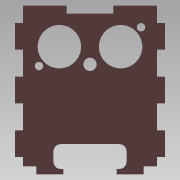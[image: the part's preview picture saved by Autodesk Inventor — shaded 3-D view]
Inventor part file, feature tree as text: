
AUTODESK INVENTOR PART (.ipt)
format: ipt  version: 2015 SP1 (Build 190203100, 203)  size: 165,888 bytes
history: native  units: mm
features: extrude x1, sketch x1
ambient origin geometry x8: Origin, YZ Plane, XZ Plane, XY Plane, X Axis, Y Axis, Z Axis, Center Point
bodies: Solid1 (feature_tree)
feature tree (2):
  extrude  "Extrusion1"  Depth=3.0mm
  sketch  "Sketch1"  dims[d0=10.0mm d1=3.0mm d2=20.0mm d4=15.0mm d5=20.0mm d7=15.0mm d14=10.0mm d15=90.0deg d16=20.0mm d18=20.0mm d19=20.0mm d21=20.0mm d24=3.0mm d25=0.0mm d26=3.0mm]
